# Revit family: Sidewall_Propeller_Fan-Carnes-LRBK-K_Series
name_source: partatom
category: Mechanical Equipment
revit_build: Autodesk Revit MEP 2012 (Build: 20110309_2315(x64)
units: mm (PartAtom-declared; Revit-internal decimal feet)

## types (7) — shared parameters
04 CSI = 23 34 16
95 CSI = 15830
Assembly Code = D3040200
Catalog URL = http://www.carnes.com
Default Elevation = 48"
Description = K Series SideWall Propellar Fan
Flow Rate = 0 CFM
IOM Instructions URL = http://www.carnes.com
Manufacturer = CARNES COMPANY
Manufacturer Fax = 608-845-6470
Material = Cast Aluminum
Parts List URL = http://www.carnes.com
Product Page URL = http://www.carnes.com
Spec Sheet URL = http://www.carnes.com
Subcategory = Sidewall Propeller Fan
Support Weight Less Motor = 0"
URL = http://www.carnes.com
Unit = Aluminum-Carnes-Spun-Brushed
ecoScorecard Product Page = http://ecoscorecard.com
zero-valued in all types: Rated CFM

## per-type parameters (varying)
| type | A | BS | CS | D | E | F Dia | Wgt. less Mtr. |
| LRBK24 | 30" | 22" | 19 7/8" | 2 1/8" | 3 1/2" | 24 1/2" | 100lbs.-46Kg. |
| LRBK30 | 36" | 22" | 19 7/8" | 2 1/8" | 4 1/4" | 30 1/2" | 112lbs.-51Kg. |
| LRBK36 | 42" | 22" | 19 7/8" | 2 1/8" | 4 1/4" | 36 1/2" | 126lbs.-57Kg. |
| LRBK42 | 48" | 26" | 23 7/8" | 2 1/8" | 4 3/4" | 42 1/2" | 136lbs.-62Kg. |
| LRBK48 | 54" | 29" | 26 7/8" | 2 1/8" | 4 3/4" | 48 1/2" | 161lbs.-73Kg. |
| LRBK54 | 60" | 32" | 29 1/4" | 2 3/4" | 5" | 55 1/2" | 225lbs.-102Kg. |
| LRBK60 | 66" | 34" | 31 1/4" | 2 3/4" | 5 1/2" | 61 3/4" | 270lbs.-122Kg. |

note: column(s) folded — value = type name in every type: Model

## geometry (parser evidence)
native form markers: Blend x4, Sweep x9
no freeform markers — native parametric forms only
